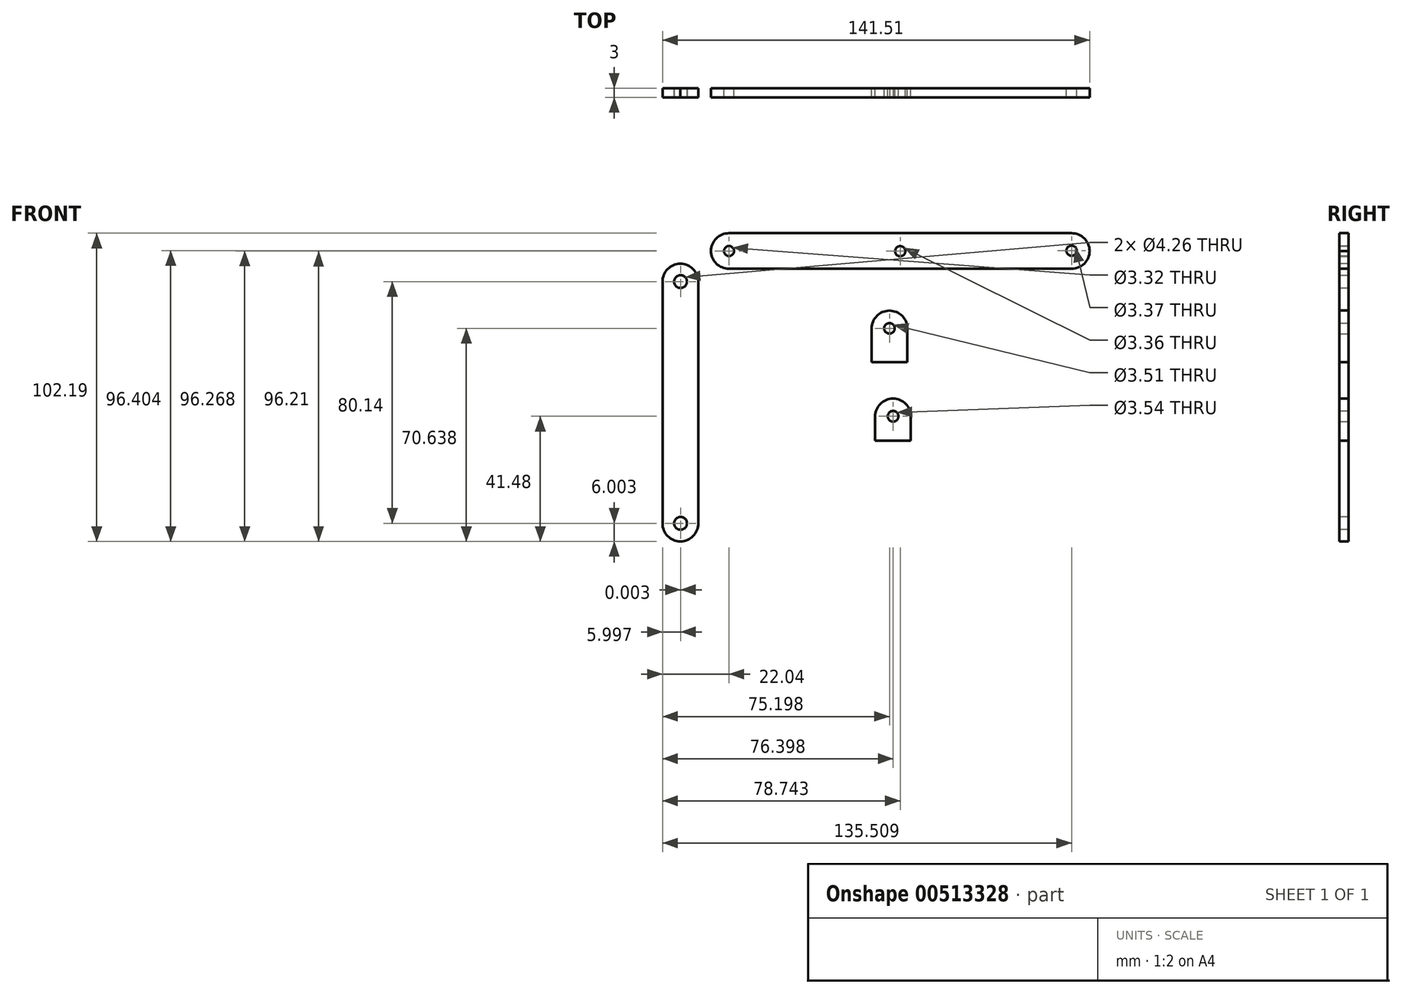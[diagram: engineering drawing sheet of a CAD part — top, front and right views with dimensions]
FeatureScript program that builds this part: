
annotation { "Feature Type Name" : "Feature", "Feature Type Description" : "" }
export const myFeature = defineFeature(function(context is Context, id is Id, definition is map)
    precondition{}
    {
        {
            var Q0;
            Q0=qCreatedBy(makeId("Front.planeOp"),FACE);
            var sketch = newSketch(context, id + "F0", { "sketchPlane" : qUnion([Q0])});
            skLineSegment(sketch, "E0", {"start": v(-61.57, 45.26) * mm, "end": v(-61.57, -46.79) * mm});
            skLineSegment(sketch, "E1", {"start": v(-61.57, 45.26) * mm, "end": v(-49.68, 45.26) * mm});
            skLineSegment(sketch, "E2", {"start": v(-61.57, -46.79) * mm, "end": v(-49.68, -46.79) * mm});
            skLineSegment(sketch, "E3", {"start": v(-49.68, 45.26) * mm, "end": v(-49.68, -46.79) * mm});
            skSolve(sketch);
        }
        {
            var Q0;
            Q0=makeQuery(id+"F0.imprint","IMPRINT",FACE,{"disambiguationData":[TD([[makeQuery(id+"F0.imprint","IMPRINT",EDGE,{"derivedFrom":sQuery(id+"F0.wireOp",EDGE,"E0")}),1.0]])]});
            extrude(context, id + "F1", {"entities" : qUnion([Q0]), "depth" : 3 * mm});
        }
        {
            var Q0;
            Q0=makeQuery(id+"F1.opExtrude","SWEPT_EDGE",EDGE,{"disambiguationData":[OSD([sQuery(id+"F0.wireOp",EDGE,"E0"),sQuery(id+"F0.wireOp",EDGE,"E1")])]});
            var Q1;
            Q1=makeQuery(id+"F1.opExtrude","SWEPT_EDGE",EDGE,{"disambiguationData":[OSD([sQuery(id+"F0.wireOp",EDGE,"E1"),sQuery(id+"F0.wireOp",EDGE,"E3")])]});
            fillet(context, id + "F2", {"entities" : qUnion([Q0, Q1]), "radius" : 6 * mm, "tangentPropagation" : true, "allowEdgeOverflow" : false});
        }
        {
            var Q0;
            Q0=makeQuery(id+"F1.opExtrude","SWEPT_EDGE",EDGE,{"disambiguationData":[OSD([sQuery(id+"F0.wireOp",EDGE,"E2"),sQuery(id+"F0.wireOp",EDGE,"E3")])]});
            var Q1;
            Q1=makeQuery(id+"F1.opExtrude","SWEPT_EDGE",EDGE,{"disambiguationData":[OSD([sQuery(id+"F0.wireOp",EDGE,"E0"),sQuery(id+"F0.wireOp",EDGE,"E2")])]});
            fillet(context, id + "F3", {"entities" : qUnion([Q0, Q1]), "radius" : 6 * mm, "tangentPropagation" : true, "allowEdgeOverflow" : false});
        }
        {
            var Q0;
            Q0=qCreatedBy(makeId("Front.planeOp"),FACE);
            var sketch = newSketch(context, id + "F4", { "sketchPlane" : qUnion([Q0])});
            skCircle(sketch, "E4", {"center": v(-55.57, 39.35) * mm, "radius": 5.9 * mm});
            skCircle(sketch, "E5", {"center": v(-55.57, 39.35) * mm, "radius": 2.13 * mm});
            skSolve(sketch);
        }
        {
            var Q0;
            Q0=makeQuery(id+"F4.imprint","IMPRINT",FACE,{"disambiguationData":[TD([[makeQuery(id+"F4.imprint","IMPRINT",EDGE,{"derivedFrom":sQuery(id+"F4.wireOp",EDGE,"E5")}),1.0]])]});
            extrude(context, id + "F5", {"entities" : qUnion([Q0]), "operationType" : NewBodyOperationType.REMOVE, "depth" : 25 * mm});
        }
        {
            var Q0;
            Q0=makeQuery(id+"F1.opExtrude","CAP_FACE",FACE,{"disambiguationData":[OSD([sQuery(id+"F0.wireOp",EDGE,"E0"),sQuery(id+"F0.wireOp",EDGE,"E1"),sQuery(id+"F0.wireOp",EDGE,"E2"),sQuery(id+"F0.wireOp",EDGE,"E3")])],"isStart":false});
            var sketch = newSketch(context, id + "F6", { "sketchPlane" : qUnion([Q0])});
            skCircle(sketch, "E6", {"center": v(-55.57, -40.79) * mm, "radius": 5.97 * mm});
            skCircle(sketch, "E7", {"center": v(-55.57, -40.79) * mm, "radius": 2.13 * mm});
            skSolve(sketch);
        }
        {
            var Q0;
            Q0=makeQuery(id+"F6.imprint","IMPRINT",FACE,{"disambiguationData":[TD([[makeQuery(id+"F6.imprint","IMPRINT",EDGE,{"derivedFrom":sQuery(id+"F6.wireOp",EDGE,"E7")}),1.0]])]});
            var Q1;
            Q1=sQuery(id+"F6.wireOp",EDGE,"E7");
            extrude(context, id + "F7", {"entities" : qUnion([Q0]), "operationType" : NewBodyOperationType.REMOVE, "surfaceEntities" : qUnion([Q1]), "oppositeDirection" : true, "depth" : 11.5 * mm});
        }
        {
            var Q0;
            Q0=qCreatedBy(makeId("Front.planeOp"),FACE);
            var sketch = newSketch(context, id + "F8", { "sketchPlane" : qUnion([Q0])});
            skLineSegment(sketch, "E8", {"start": v(-45.53, 55.4) * mm, "end": v(79.94, 55.4) * mm});
            skLineSegment(sketch, "E9", {"start": v(-45.53, 55.4) * mm, "end": v(-45.53, 43.61) * mm});
            skLineSegment(sketch, "E10", {"start": v(79.94, 55.4) * mm, "end": v(79.94, 43.61) * mm});
            skLineSegment(sketch, "E11", {"start": v(79.94, 43.61) * mm, "end": v(-45.53, 43.61) * mm});
            skSolve(sketch);
        }
        {
            var Q0;
            Q0=makeQuery(id+"F8.imprint","IMPRINT",FACE,{"disambiguationData":[TD([[makeQuery(id+"F8.imprint","IMPRINT",EDGE,{"derivedFrom":sQuery(id+"F8.wireOp",EDGE,"E8")}),-1.0]])]});
            extrude(context, id + "F9", {"entities" : qUnion([Q0]), "depth" : 3 * mm});
        }
        {
            var Q0;
            Q0=makeQuery(id+"F9.opExtrude","SWEPT_EDGE",EDGE,{"disambiguationData":[OSD([sQuery(id+"F8.wireOp",EDGE,"E8"),sQuery(id+"F8.wireOp",EDGE,"E9")])]});
            var Q1;
            Q1=makeQuery(id+"F9.opExtrude","SWEPT_EDGE",EDGE,{"disambiguationData":[OSD([sQuery(id+"F8.wireOp",EDGE,"E9"),sQuery(id+"F8.wireOp",EDGE,"E11")])]});
            fillet(context, id + "F10", {"entities" : qUnion([Q0, Q1]), "radius" : 6 * mm, "tangentPropagation" : true, "allowEdgeOverflow" : false});
        }
        {
            var Q0;
            Q0=makeQuery(id+"F9.opExtrude","SWEPT_EDGE",EDGE,{"disambiguationData":[OSD([sQuery(id+"F8.wireOp",EDGE,"E8"),sQuery(id+"F8.wireOp",EDGE,"E10")])]});
            var Q1;
            Q1=makeQuery(id+"F9.opExtrude","SWEPT_EDGE",EDGE,{"disambiguationData":[OSD([sQuery(id+"F8.wireOp",EDGE,"E10"),sQuery(id+"F8.wireOp",EDGE,"E11")])]});
            fillet(context, id + "F11", {"entities" : qUnion([Q0, Q1]), "radius" : 6 * mm, "tangentPropagation" : true, "allowEdgeOverflow" : false});
        }
        {
            var Q0;
            Q0=qCreatedBy(makeId("Front.planeOp"),FACE);
            var sketch = newSketch(context, id + "F12", { "sketchPlane" : qUnion([Q0])});
            skCircle(sketch, "E12", {"center": v(-39.53, 49.48) * mm, "radius": 5.9 * mm});
            skCircle(sketch, "E13", {"center": v(-39.53, 49.48) * mm, "radius": 1.66 * mm});
            skSolve(sketch);
        }
        {
            var Q0;
            Q0=makeQuery(id+"F12.imprint","IMPRINT",FACE,{"disambiguationData":[TD([[makeQuery(id+"F12.imprint","IMPRINT",EDGE,{"derivedFrom":sQuery(id+"F12.wireOp",EDGE,"E13")}),1.0]])]});
            var Q1;
            Q1=sQuery(id+"F12.wireOp",EDGE,"E13");
            extrude(context, id + "F13", {"entities" : qUnion([Q0]), "operationType" : NewBodyOperationType.REMOVE, "surfaceEntities" : qUnion([Q1]), "depth" : 48.8 * mm});
        }
        {
            var Q0;
            Q0=makeQuery(id+"F9.opExtrude","CAP_FACE",FACE,{"disambiguationData":[OSD([sQuery(id+"F8.wireOp",EDGE,"E8"),sQuery(id+"F8.wireOp",EDGE,"E9"),sQuery(id+"F8.wireOp",EDGE,"E10"),sQuery(id+"F8.wireOp",EDGE,"E11")])],"isStart":true});
            var sketch = newSketch(context, id + "F14", { "sketchPlane" : qUnion([Q0])});
            skCircle(sketch, "E14", {"center": v(-73.94, 49.61) * mm, "radius": 5.82 * mm});
            skCircle(sketch, "E15", {"center": v(-73.94, 49.61) * mm, "radius": 1.69 * mm});
            skSolve(sketch);
        }
        {
            var Q0;
            Q0=makeQuery(id+"F14.imprint","IMPRINT",FACE,{"disambiguationData":[TD([[makeQuery(id+"F14.imprint","IMPRINT",EDGE,{"derivedFrom":sQuery(id+"F14.wireOp",EDGE,"E15")}),1.0]])]});
            extrude(context, id + "F15", {"entities" : qUnion([Q0]), "operationType" : NewBodyOperationType.REMOVE, "oppositeDirection" : true, "depth" : 13.8 * mm});
        }
        {
            var Q0;
            Q0=qCreatedBy(makeId("Front.planeOp"),FACE);
            var sketch = newSketch(context, id + "F16", { "sketchPlane" : qUnion([Q0])});
            skCircle(sketch, "E16", {"center": v(17.17, 49.42) * mm, "radius": 5.88 * mm});
            skCircle(sketch, "E17", {"center": v(17.17, 49.42) * mm, "radius": 1.68 * mm});
            skSolve(sketch);
        }
        {
            var Q0;
            Q0=makeQuery(id+"F16.imprint","IMPRINT",FACE,{"disambiguationData":[TD([[makeQuery(id+"F16.imprint","IMPRINT",EDGE,{"derivedFrom":sQuery(id+"F16.wireOp",EDGE,"E17")}),1.0]])]});
            var Q1;
            Q1=sQuery(id+"F16.wireOp",EDGE,"E17");
            extrude(context, id + "F17", {"entities" : qUnion([Q0]), "operationType" : NewBodyOperationType.REMOVE, "surfaceEntities" : qUnion([Q1]), "depth" : 14.7 * mm});
        }
        {
            var Q0;
            Q0=qCreatedBy(makeId("Front.planeOp"),FACE);
            var sketch = newSketch(context, id + "F18", { "sketchPlane" : qUnion([Q0])});
            skLineSegment(sketch, "E18", {"start": v(7.7, 29.73) * mm, "end": v(7.7, 12.7) * mm});
            skLineSegment(sketch, "E19", {"start": v(7.7, 29.73) * mm, "end": v(19.54, 29.73) * mm});
            skLineSegment(sketch, "E20", {"start": v(7.7, 12.7) * mm, "end": v(19.54, 12.7) * mm});
            skLineSegment(sketch, "E21", {"start": v(19.54, 12.7) * mm, "end": v(19.54, 29.73) * mm});
            skSolve(sketch);
        }
        {
            var Q0;
            Q0=makeQuery(id+"F18.imprint","IMPRINT",FACE,{"disambiguationData":[TD([[makeQuery(id+"F18.imprint","IMPRINT",EDGE,{"derivedFrom":sQuery(id+"F18.wireOp",EDGE,"E18")}),1.0]])]});
            extrude(context, id + "F19", {"entities" : qUnion([Q0]), "depth" : 3 * mm});
        }
        {
            var Q0;
            Q0=makeQuery(id+"F19.opExtrude","SWEPT_EDGE",EDGE,{"disambiguationData":[OSD([sQuery(id+"F18.wireOp",EDGE,"E19"),sQuery(id+"F18.wireOp",EDGE,"E21")])]});
            var Q1;
            Q1=makeQuery(id+"F19.opExtrude","SWEPT_EDGE",EDGE,{"disambiguationData":[OSD([sQuery(id+"F18.wireOp",EDGE,"E18"),sQuery(id+"F18.wireOp",EDGE,"E19")])]});
            fillet(context, id + "F20", {"entities" : qUnion([Q0, Q1]), "radius" : 6 * mm, "tangentPropagation" : true, "allowEdgeOverflow" : false});
        }
        {
            var Q0;
            Q0=qCreatedBy(makeId("Front.planeOp"),FACE);
            var sketch = newSketch(context, id + "F21", { "sketchPlane" : qUnion([Q0])});
            skCircle(sketch, "E22", {"center": v(13.63, 23.85) * mm, "radius": 5.76 * mm});
            skCircle(sketch, "E23", {"center": v(13.63, 23.85) * mm, "radius": 1.75 * mm});
            skSolve(sketch);
        }
        {
            var Q0;
            Q0=makeQuery(id+"F21.imprint","IMPRINT",FACE,{"disambiguationData":[TD([[makeQuery(id+"F21.imprint","IMPRINT",EDGE,{"derivedFrom":sQuery(id+"F21.wireOp",EDGE,"E23")}),1.0]])]});
            var Q1;
            Q1=sQuery(id+"F21.wireOp",EDGE,"E23");
            extrude(context, id + "F22", {"entities" : qUnion([Q0]), "operationType" : NewBodyOperationType.REMOVE, "surfaceEntities" : qUnion([Q1]), "depth" : 6.9 * mm});
        }
        {
            var Q0;
            Q0=qCreatedBy(makeId("Front.planeOp"),FACE);
            var sketch = newSketch(context, id + "F23", { "sketchPlane" : qUnion([Q0])});
            skLineSegment(sketch, "E24", {"start": v(20.72, -13.45) * mm, "end": v(20.72, 0.57) * mm});
            skLineSegment(sketch, "E25", {"start": v(20.72, 0.57) * mm, "end": v(8.87, 0.57) * mm});
            skLineSegment(sketch, "E26", {"start": v(20.72, -13.45) * mm, "end": v(8.87, -13.45) * mm});
            skLineSegment(sketch, "E27", {"start": v(8.87, -13.45) * mm, "end": v(8.87, 0.57) * mm});
            skSolve(sketch);
        }
        {
            var Q0;
            Q0=makeQuery(id+"F23.imprint","IMPRINT",FACE,{"disambiguationData":[TD([[makeQuery(id+"F23.imprint","IMPRINT",EDGE,{"derivedFrom":sQuery(id+"F23.wireOp",EDGE,"E24")}),1.0]])]});
            extrude(context, id + "F24", {"entities" : qUnion([Q0]), "depth" : 3 * mm});
        }
        {
            var Q0;
            Q0=makeQuery(id+"F24.opExtrude","SWEPT_EDGE",EDGE,{"disambiguationData":[OSD([sQuery(id+"F23.wireOp",EDGE,"E25"),sQuery(id+"F23.wireOp",EDGE,"E27")])]});
            var Q1;
            Q1=makeQuery(id+"F24.opExtrude","SWEPT_EDGE",EDGE,{"disambiguationData":[OSD([sQuery(id+"F23.wireOp",EDGE,"E24"),sQuery(id+"F23.wireOp",EDGE,"E25")])]});
            fillet(context, id + "F25", {"entities" : qUnion([Q0, Q1]), "radius" : 6 * mm, "tangentPropagation" : true, "allowEdgeOverflow" : false});
        }
        {
            var Q0;
            Q0=qCreatedBy(makeId("Front.planeOp"),FACE);
            var sketch = newSketch(context, id + "F26", { "sketchPlane" : qUnion([Q0])});
            skCircle(sketch, "E28", {"center": v(14.83, -5.3) * mm, "radius": 5.87 * mm});
            skCircle(sketch, "E29", {"center": v(14.83, -5.3) * mm, "radius": 1.77 * mm});
            skSolve(sketch);
        }
        {
            var Q0;
            Q0=makeQuery(id+"F26.imprint","IMPRINT",FACE,{"disambiguationData":[TD([[makeQuery(id+"F26.imprint","IMPRINT",EDGE,{"derivedFrom":sQuery(id+"F26.wireOp",EDGE,"E29")}),1.0]])]});
            var Q1;
            Q1=sQuery(id+"F26.wireOp",EDGE,"E29");
            extrude(context, id + "F27", {"entities" : qUnion([Q0]), "operationType" : NewBodyOperationType.REMOVE, "surfaceEntities" : qUnion([Q1]), "depth" : 16.9 * mm, "offsetDistance" : 25 * mm});
        }
    });
